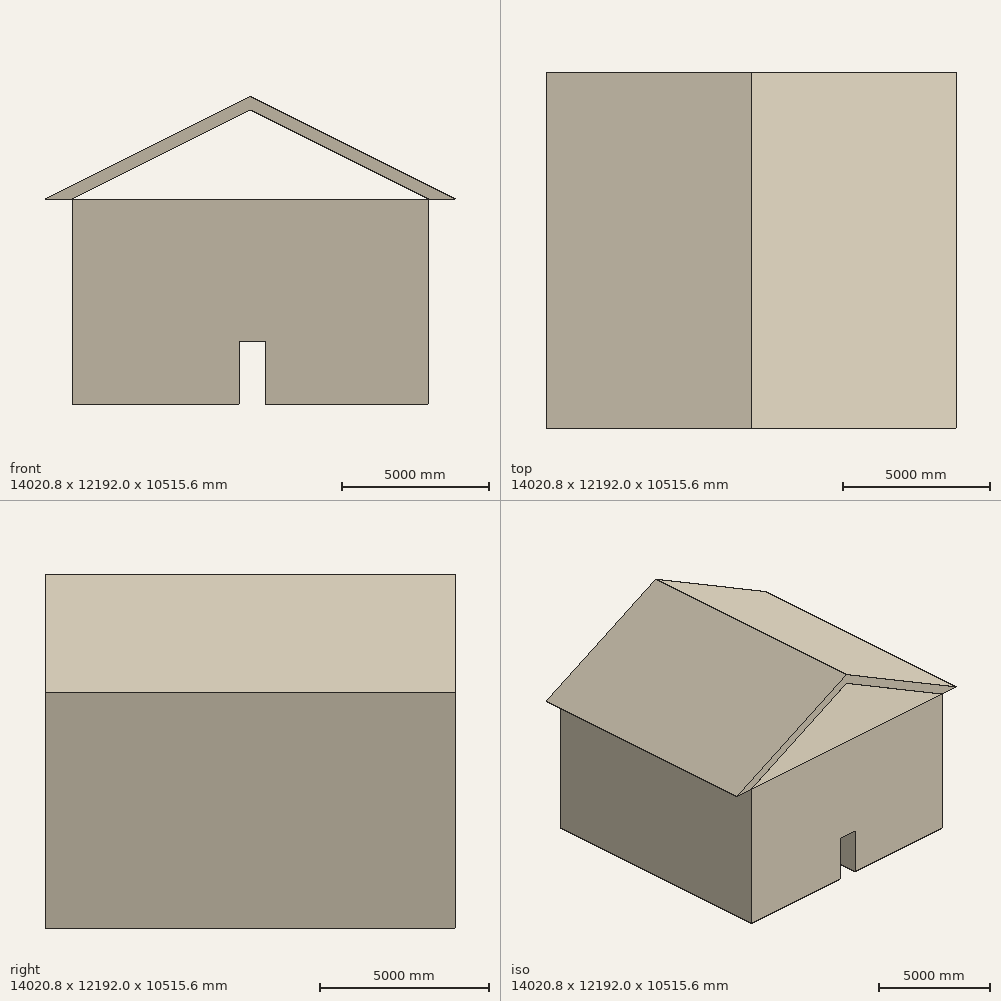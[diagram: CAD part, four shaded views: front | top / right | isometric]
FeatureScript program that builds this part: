
annotation { "Feature Type Name" : "Feature", "Feature Type Description" : "" }
export const myFeature = defineFeature(function(context is Context, id is Id, definition is map)
    precondition{}
    {
        {
            var Q0;
            Q0=qCreatedBy(makeId("Front.planeOp"),FACE);
            var sketch = newSketch(context, id + "F0", { "sketchPlane" : qUnion([Q0])});
            skLineSegment(sketch, "E0", {"start": v(0, 0) * mm, "end": v(-6096, 0) * mm});
            skLineSegment(sketch, "E1", {"start": v(0, 0) * mm, "end": v(6096, 0) * mm});
            skLineSegment(sketch, "E2", {"start": v(0, 0) * mm, "end": v(0, 3048) * mm});
            skLineSegment(sketch, "E3", {"start": v(0, 3048) * mm, "end": v(-6096, 0) * mm});
            skLineSegment(sketch, "E4", {"start": v(0, 3048) * mm, "end": v(6096, 0) * mm});
            skLineSegment(sketch, "E5", {"start": v(-6096, 0) * mm, "end": v(-7010.4, 0) * mm});
            skLineSegment(sketch, "E6", {"start": v(6096, 0) * mm, "end": v(7010.4, 0) * mm});
            skLineSegment(sketch, "E7", {"start": v(0, 3048) * mm, "end": v(0, 3505.2) * mm});
            skLineSegment(sketch, "E8", {"start": v(0, 3505.2) * mm, "end": v(-7010.4, 0) * mm});
            skLineSegment(sketch, "E9", {"start": v(0, 3505.2) * mm, "end": v(7010.4, 0) * mm});
            skLineSegment(sketch, "E10", {"start": v(-6096, 0) * mm, "end": v(-6096, -7315.2) * mm});
            skLineSegment(sketch, "E11", {"start": v(6096, 0) * mm, "end": v(6096, -7315.2) * mm});
            skLineSegment(sketch, "E12", {"start": v(-6096, -7315.2) * mm, "end": v(6096, -7315.2) * mm});
            skLineSegment(sketch, "E13", {"start": v(-6096, -7315.2) * mm, "end": v(-6096, -7010.4) * mm});
            skLineSegment(sketch, "E14", {"start": v(6096, -7315.2) * mm, "end": v(6096, -7010.4) * mm});
            skLineSegment(sketch, "E15", {"start": v(6096, -7010.4) * mm, "end": v(-6096, -7010.4) * mm});
            skLineSegment(sketch, "E16", {"start": v(0, 0) * mm, "end": v(0, -7010.4) * mm});
            skLineSegment(sketch, "E17", {"start": v(522.97, -7010.4) * mm, "end": v(-391.43, -7010.4) * mm});
            skLineSegment(sketch, "E18", {"start": v(522.97, -7010.4) * mm, "end": v(522.97, -4876.8) * mm});
            skLineSegment(sketch, "E19", {"start": v(522.97, -4876.8) * mm, "end": v(-391.43, -4876.8) * mm});
            skLineSegment(sketch, "E20", {"start": v(-391.43, -4876.8) * mm, "end": v(-391.43, -7010.4) * mm});
            skSolve(sketch);
        }
        {
            var Q0;
            Q0=makeQuery(id+"F0.imprint","IMPRINT",FACE,{"disambiguationData":[TD([[makeQuery(id+"F0.imprint","IMPRINT",EDGE,{"derivedFrom":sQuery(id+"F0.wireOp",EDGE,"E3")}),-1.0]])]});
            var Q1;
            Q1=makeQuery(id+"F0.imprint","IMPRINT",FACE,{"disambiguationData":[TD([[makeQuery(id+"F0.imprint","IMPRINT",EDGE,{"derivedFrom":sQuery(id+"F0.wireOp",EDGE,"E4")}),1.0]])]});
            var Q2;
            {var subQ1=sQuery(id+"F0.wireOp",EDGE,"E0");Q2=makeQuery(id+"F0.imprint","IMPRINT",FACE,{"disambiguationData":[TD([[makeQuery(id+"F0.imprint","IMPRINT",EDGE,{"derivedFrom":subQ1}),1.0]])]});}
            var Q3;
            {var subQ1=sQuery(id+"F0.wireOp",EDGE,"E1");Q3=makeQuery(id+"F0.imprint","IMPRINT",FACE,{"disambiguationData":[TD([[makeQuery(id+"F0.imprint","IMPRINT",EDGE,{"derivedFrom":subQ1}),-1.0]])]});}
            extrude(context, id + "F1", {"entities" : qUnion([Q0, Q1, Q2, Q3]), "endBound" : BoundingType.SYMMETRIC, "depth" : 12192 * mm, "offsetDistance" : 30.48 * mm});
        }
        {
            var Q0;
            Q0=sQuery(id+"F0.wireOp",EDGE,"E12");
            var Q1;
            Q1=sQuery(id+"F0.wireOp",EDGE,"E15");
            extrude(context, id + "F2", {"bodyType" : ToolBodyType.SURFACE, "surfaceEntities" : qUnion([Q0, Q1]), "endBound" : BoundingType.SYMMETRIC, "depth" : 16154.4 * mm, "offsetDistance" : 30.48 * mm});
        }
    });
